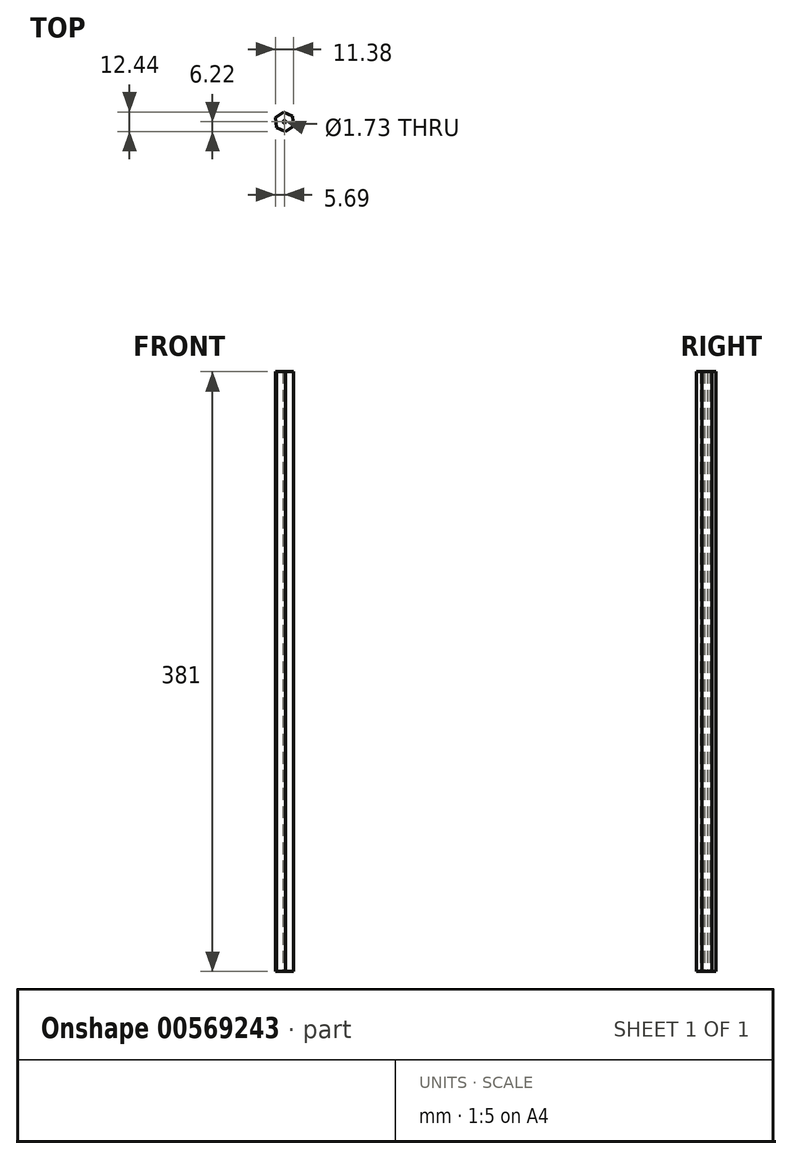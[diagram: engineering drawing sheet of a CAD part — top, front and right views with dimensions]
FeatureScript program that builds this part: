
annotation { "Feature Type Name" : "Feature", "Feature Type Description" : "" }
export const myFeature = defineFeature(function(context is Context, id is Id, definition is map)
    precondition{}
    {
        {
            var Q0;
            Q0=qCreatedBy(makeId("Top.planeOp"),FACE);
            var sketch = newSketch(context, id + "F0", { "sketchPlane" : qUnion([Q0])});
            skCircle(sketch, "E0", {"center": v(0, 0) * mm, "radius": 0.86 * mm});
            skSolve(sketch);
        }
        {
            var Q0;
            Q0=qCreatedBy(makeId("Top.planeOp"),FACE);
            var sketch = newSketch(context, id + "F1", { "sketchPlane" : qUnion([Q0])});
            skCircle(sketch, "E1.cCircle", {"center": v(0, 0) * mm, "radius": 5.41 * mm, "construction": true});
            skLineSegment(sketch, "E1.0", {"start": v(5.7, -2.59) * mm, "end": v(0.6, -6.22) * mm});
            skLineSegment(sketch, "E1.1", {"start": v(0.6, -6.22) * mm, "end": v(-5.09, -3.63) * mm});
            skLineSegment(sketch, "E1.2", {"start": v(-5.09, -3.63) * mm, "end": v(-5.7, 2.59) * mm});
            skLineSegment(sketch, "E1.3", {"start": v(-5.7, 2.59) * mm, "end": v(-0.6, 6.22) * mm});
            skLineSegment(sketch, "E1.4", {"start": v(-0.6, 6.22) * mm, "end": v(5.09, 3.63) * mm});
            skLineSegment(sketch, "E1.5", {"start": v(5.09, 3.63) * mm, "end": v(5.7, -2.59) * mm});
            skPoint(sketch, "E1.0.midPoint", {"position": v(3.15, -4.4) * mm});
            skSolve(sketch);
        }
        {
            var Q0;
            Q0=makeQuery(id+"F1.imprint","IMPRINT",FACE,{"disambiguationData":[TD([[makeQuery(id+"F1.imprint","IMPRINT",EDGE,{"derivedFrom":sQuery(id+"F1.wireOp",EDGE,"E1.0")}),-1.0]])]});
            extrude(context, id + "F2", {"entities" : qUnion([Q0]), "depth" : 381 * mm, "offsetDistance" : 25.4 * mm});
        }
        {
            var Q0;
            Q0 = qSketchRegion(id + "F0", true);
            extrude(context, id + "F3", {"entities" : qUnion([Q0]), "operationType" : NewBodyOperationType.REMOVE, "oppositeDirection" : true, "depth" : 0 * mm, "offsetDistance" : 25.4 * mm, "hasSecondDirection" : true, "secondDirectionOppositeDirection" : false, "secondDirectionDepth" : 381 * mm});
        }
    });
